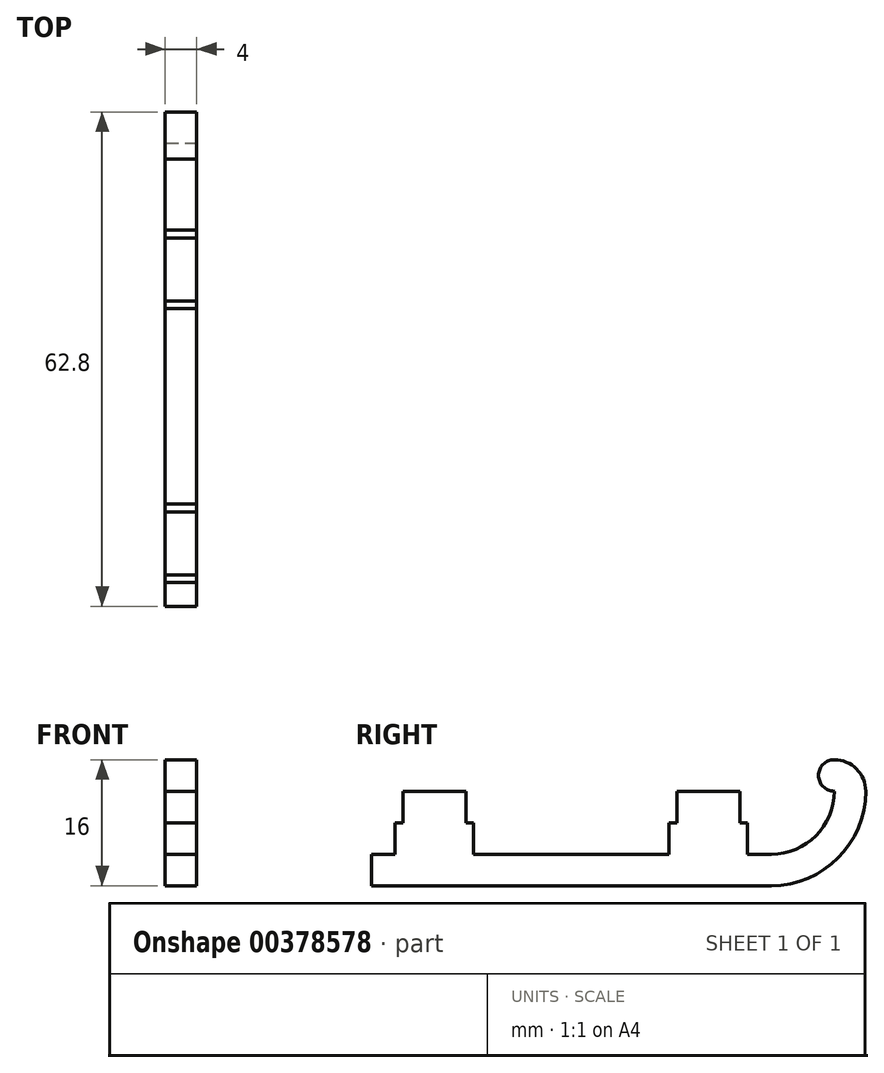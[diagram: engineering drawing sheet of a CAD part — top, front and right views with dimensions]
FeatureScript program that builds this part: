
annotation { "Feature Type Name" : "Feature", "Feature Type Description" : "" }
export const myFeature = defineFeature(function(context is Context, id is Id, definition is map)
    precondition{}
    {
        {
            var Q0;
            Q0=qCreatedBy(makeId("Right.planeOp"),FACE);
            var sketch = newSketch(context, id + "F0", { "sketchPlane" : qUnion([Q0])});
            skLineSegment(sketch, "E0.bottom", {"start": v(0, 0) * mm, "end": v(50.8, 0) * mm});
            skLineSegment(sketch, "E0.top", {"start": v(0, 4) * mm, "end": v(50.8, 4) * mm});
            skLineSegment(sketch, "E0.left", {"start": v(0, 0) * mm, "end": v(0, 4) * mm});
            skLineSegment(sketch, "E1.bottom", {"start": v(3, 4) * mm, "end": v(13, 4) * mm});
            skLineSegment(sketch, "E1.top", {"start": v(3, 8) * mm, "end": v(13, 8) * mm});
            skLineSegment(sketch, "E1.left", {"start": v(3, 4) * mm, "end": v(3, 8) * mm});
            skLineSegment(sketch, "E1.right", {"start": v(13, 4) * mm, "end": v(13, 8) * mm});
            skLineSegment(sketch, "E2.bottom", {"start": v(37.8, 4) * mm, "end": v(47.8, 4) * mm});
            skLineSegment(sketch, "E2.top", {"start": v(37.8, 8) * mm, "end": v(47.8, 8) * mm});
            skLineSegment(sketch, "E2.left", {"start": v(37.8, 4) * mm, "end": v(37.8, 8) * mm});
            skLineSegment(sketch, "E2.right", {"start": v(47.8, 4) * mm, "end": v(47.8, 8) * mm});
            skLineSegment(sketch, "E3", {"start": v(50.8, 4) * mm, "end": v(50.8, 26.68) * mm, "construction": true});
            skLineSegment(sketch, "E4.bottom", {"start": v(4, 8) * mm, "end": v(12, 8) * mm});
            skLineSegment(sketch, "E4.top", {"start": v(4, 12) * mm, "end": v(12, 12) * mm});
            skLineSegment(sketch, "E4.left", {"start": v(4, 8) * mm, "end": v(4, 12) * mm});
            skLineSegment(sketch, "E4.right", {"start": v(12, 8) * mm, "end": v(12, 12) * mm});
            skLineSegment(sketch, "E5.bottom", {"start": v(38.8, 8) * mm, "end": v(46.8, 8) * mm});
            skLineSegment(sketch, "E5.top", {"start": v(38.8, 12) * mm, "end": v(46.8, 12) * mm});
            skLineSegment(sketch, "E5.left", {"start": v(38.8, 8) * mm, "end": v(38.8, 12) * mm});
            skLineSegment(sketch, "E5.right", {"start": v(46.8, 8) * mm, "end": v(46.8, 12) * mm});
            skPoint(sketch, "E6", {"position": v(50.8, 12) * mm});
            skArc(sketch, "E7", {"start": v(50.8, 4) * mm, "mid": v(56.46, 6.34) * mm, "end": v(58.8, 12) * mm});
            skArc(sketch, "E8", {"start": v(50.8, 0) * mm, "mid": v(59.29, 3.51) * mm, "end": v(62.8, 12) * mm});
            skArc(sketch, "E9", {"start": v(62.8, 12) * mm, "mid": v(61.63, 14.83) * mm, "end": v(58.8, 16) * mm});
            skLineSegment(sketch, "E10", {"start": v(58.8, 16) * mm, "end": v(58.8, 12) * mm, "construction": true});
            skPoint(sketch, "E11", {"position": v(58.8, 14) * mm});
            skArc(sketch, "E12", {"start": v(58.8, 16) * mm, "mid": v(56.8, 14) * mm, "end": v(58.8, 12) * mm});
            skSolve(sketch);
        }
        {
            var Q0;
            Q0 = qSketchRegion(id + "F0", true);
            extrude(context, id + "F1", {"entities" : qUnion([Q0]), "depth" : 4 * mm});
        }
    });
